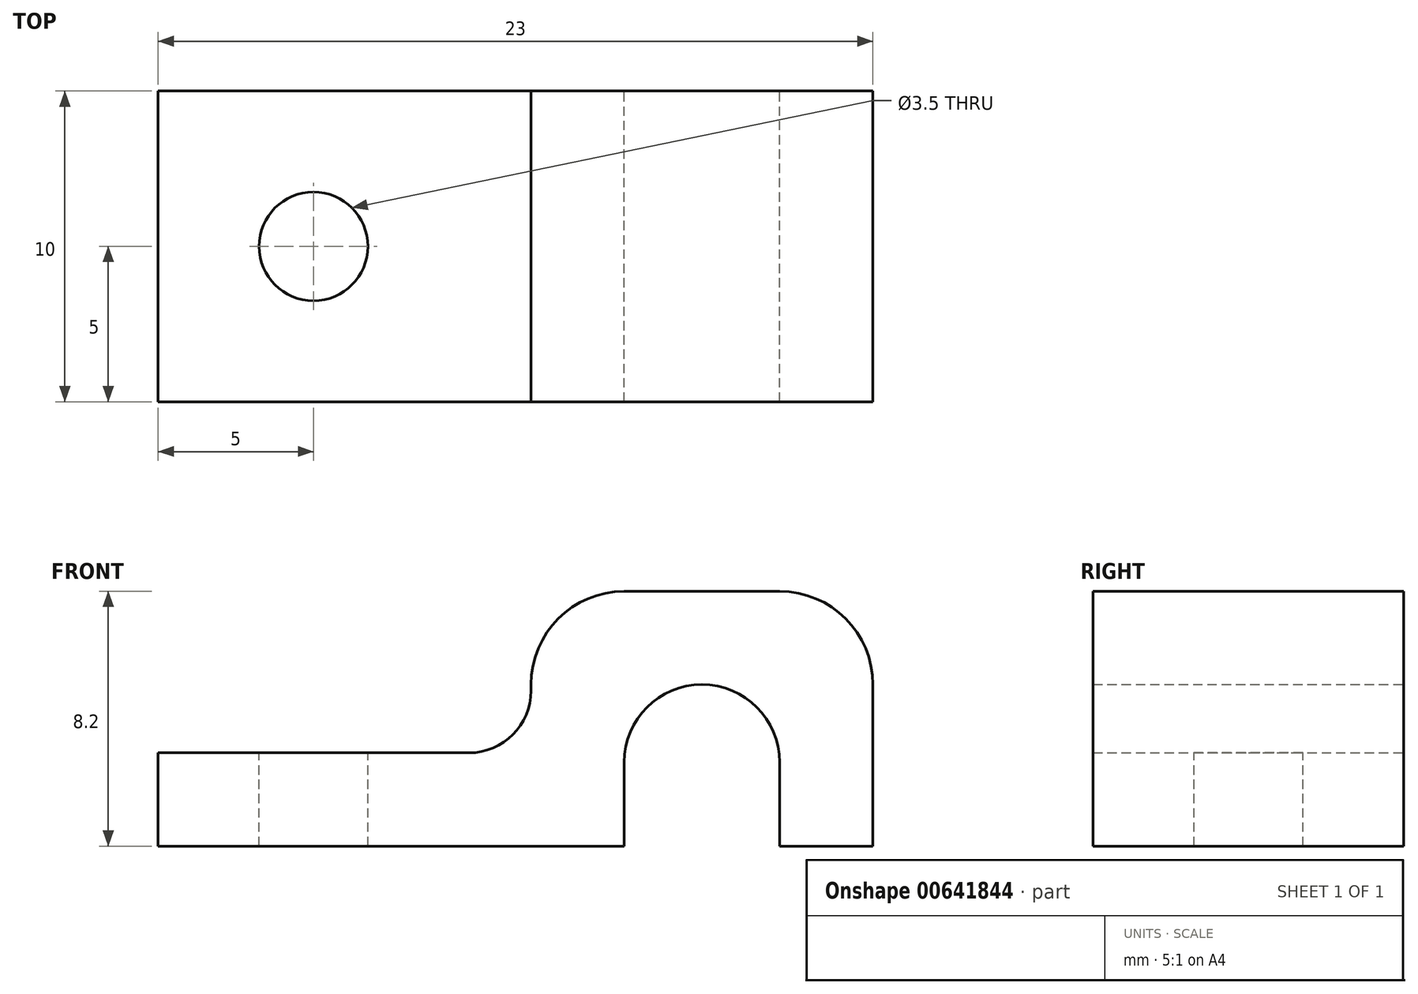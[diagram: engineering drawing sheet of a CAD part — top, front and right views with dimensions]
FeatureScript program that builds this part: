
annotation { "Feature Type Name" : "Feature", "Feature Type Description" : "" }
export const myFeature = defineFeature(function(context is Context, id is Id, definition is map)
    precondition{}
    {
        {
            var Q0;
            Q0=qCreatedBy(makeId("Front.planeOp"),FACE);
            var sketch = newSketch(context, id + "F0", { "sketchPlane" : qUnion([Q0])});
            skLineSegment(sketch, "E0", {"start": v(0, 0) * mm, "end": v(-12, 0) * mm});
            skLineSegment(sketch, "E1", {"start": v(-12, 0) * mm, "end": v(-12, 3) * mm});
            skLineSegment(sketch, "E2", {"start": v(-12, 3) * mm, "end": v(-2, 3) * mm});
            skLineSegment(sketch, "E3", {"start": v(0, 5) * mm, "end": v(0, 5.2) * mm});
            skLineSegment(sketch, "E4", {"start": v(3, 8.2) * mm, "end": v(8, 8.2) * mm});
            skLineSegment(sketch, "E5", {"start": v(11, 5.2) * mm, "end": v(11, 0) * mm});
            skLineSegment(sketch, "E6", {"start": v(11, 0) * mm, "end": v(8, 0) * mm});
            skLineSegment(sketch, "E7", {"start": v(8, 0) * mm, "end": v(8, 2.7) * mm});
            skLineSegment(sketch, "E8", {"start": v(0, 0) * mm, "end": v(3, 0) * mm});
            skLineSegment(sketch, "E9", {"start": v(3, 2.7) * mm, "end": v(3, 0) * mm});
            skCircle(sketch, "E10", {"center": v(5.5, 2.7) * mm, "radius": 2.5 * mm});
            skPoint(sketch, "E11.visualSharp", {"position": v(0, 8.2) * mm});
            skArc(sketch, "E11.filletArc", {"start": v(3, 8.2) * mm, "mid": v(0.88, 7.32) * mm, "end": v(0, 5.2) * mm});
            skPoint(sketch, "E12.visualSharp", {"position": v(11, 8.2) * mm});
            skArc(sketch, "E12.filletArc", {"start": v(11, 5.2) * mm, "mid": v(10.12, 7.32) * mm, "end": v(8, 8.2) * mm});
            skPoint(sketch, "E13.visualSharp", {"position": v(0, 3) * mm});
            skArc(sketch, "E13.filletArc", {"start": v(-2, 3) * mm, "mid": v(-0.59, 3.59) * mm, "end": v(0, 5) * mm});
            skSolve(sketch);
        }
        {
            var Q0;
            Q0=makeQuery(id+"F0.imprint","IMPRINT",FACE,{"disambiguationData":[TD([[makeQuery(id+"F0.imprint","IMPRINT",EDGE,{"derivedFrom":sQuery(id+"F0.wireOp",EDGE,"E0")}),-1.0]])]});
            extrude(context, id + "F1", {"entities" : qUnion([Q0]), "depth" : 10 * mm, "offsetDistance" : 25 * mm});
        }
        {
            var Q0;
            Q0=makeQuery(id+"F1.opExtrude","SWEPT_FACE",FACE,{"disambiguationData":[OSD([sQuery(id+"F0.wireOp",EDGE,"E2")])]});
            cPlane(context, id + "F2", {"entities" : qUnion([Q0]), "cplaneType" : CPlaneType.OFFSET, "offset" : 0 * mm, "width" : 150 * mm, "height" : 150 * mm});
        }
        {
            var Q0;
            Q0=qCreatedBy(id+"F2.planeOp",FACE);
            var sketch = newSketch(context, id + "F3", { "sketchPlane" : qUnion([Q0])});
            skLineSegment(sketch, "E14", {"start": v(-7, -12.4) * mm, "end": v(-7, 3.21) * mm, "construction": true});
            skLineSegment(sketch, "E15", {"start": v(-16.36, -5) * mm, "end": v(3.42, -5) * mm, "construction": true});
            skCircle(sketch, "E16", {"center": v(-7, -5) * mm, "radius": 1.75 * mm});
            skSolve(sketch);
        }
        {
            var Q0;
            Q0=makeQuery(id+"F3.imprint","IMPRINT",FACE,{"disambiguationData":[TD([[makeQuery(id+"F3.imprint","IMPRINT",EDGE,{"derivedFrom":sQuery(id+"F3.wireOp",EDGE,"E16")}),1.0]])]});
            extrude(context, id + "F4", {"entities" : qUnion([Q0]), "operationType" : NewBodyOperationType.REMOVE, "endBound" : BoundingType.THROUGH_ALL, "oppositeDirection" : true, "depth" : 25 * mm, "offsetDistance" : 25 * mm});
        }
    });
